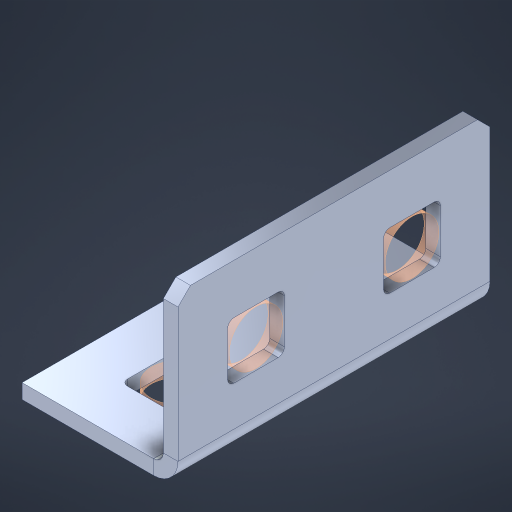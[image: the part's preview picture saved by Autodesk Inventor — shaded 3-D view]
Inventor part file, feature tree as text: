
AUTODESK INVENTOR PART (.ipt)
format: ipt  version: 2023 (Build 270158000, 158)  size: 376,832 bytes
history: native  units: in
note: dims shown in document units (in); Inventor stores cm internally (conversion verified against a paired STEP export)
features: sheet_metal_op x10, other x9, sketch x8, extrude x3, mirror x1, pattern_linear x1, chamfer x1
ambient origin geometry x8: Origin, YZ Plane, XZ Plane, XY Plane, X Axis, Y Axis, Z Axis, Center Point
bodies: Solid1 (feature_tree), Body (feature_tree)
feature tree (33):
  other  "Flange Pattern Plane"
  sheet_metal_op  "Flange Pattern"
  sheet_metal_op  "Body Pattern"
  other  "Arc Length"
  mirror  "Notch Mirror"
  pattern_linear  "Notch Pattern"  Spacing1=0.1875in  [1 undecoded]
  chamfer  "End Chamfer"
  extrude  "Half Cut"  Depth=0.0469in
  sketch  "Sketch1"  dims[d0=2.5in]
  other  "Plate1"
  sketch  "Sketch2"  dims[d1=1.0in]
  other  "Plate2"
  sheet_metal_op  "Bend1"
  sheet_metal_op  "Corner1"
  sketch  "Sketch3"  dims[d2=0.0469in]
  other  "Flange Pattern Sketch"
  sketch  "Sketch7"  dims[d3=0.0469in]
  other  "Srf1"
  other  "Srf2"
  sketch  "Sketch8"  dims[d4=0.0234in]
  sketch  "Sketch9"  dims[d5=0.0938in]
  other  "Srf91"
  sheet_metal_op  "Body Pattern Sketch"
  other  "Srf92"
  sketch  "Sketch13"  dims[d6=0.0469in]
  sketch  "Sketch14"  dims[d7=0.5in d8=90.0deg d9=0.0312in d10=0.1875in d11=0.0469in d12=0.0469in d16=0.182in d17=0.02in d18=0.0469in d19=0.0in d20=0.25in d21=0.25in d46=0.172in d47=1.0in d48=0.0in d49=0.182in d50=0.02in d51=0.25in d52=0.25in d53=0.0469in d54=0.0in d55=0.172in d56=1.0in d57=0.0in d60=0.7874in d62=0.5in d63=0.3937in d65=0.5in d85=0.1227in d86=0.1659in d88=0.04in d89=0.0469in d90=0.0in d91=0.04in d92=0.0491in d95=2.5in d96=0.04in d97=0.25in d98=45.0deg d101=0.0in d102=2.497in d131=0.5in d132=0.7874in d134=0.5in d139=0.5in]
  sheet_metal_op  "Flange Stamp"
  sheet_metal_op  "Flange Circle"
  sheet_metal_op  "Body Stamp"
  sheet_metal_op  "Body Circle"
  sheet_metal_op  "Notch"
  extrude  "ExtrusionSrf2"  Depth=0.0469in
  extrude  "ExtrusionSrf92"  Depth=0.182in
note: 1 required parameter value undecoded (feature->parameter linkage not recoverable at this tier; creation-order binding heuristic only, values carry confidence <= 0.55)
